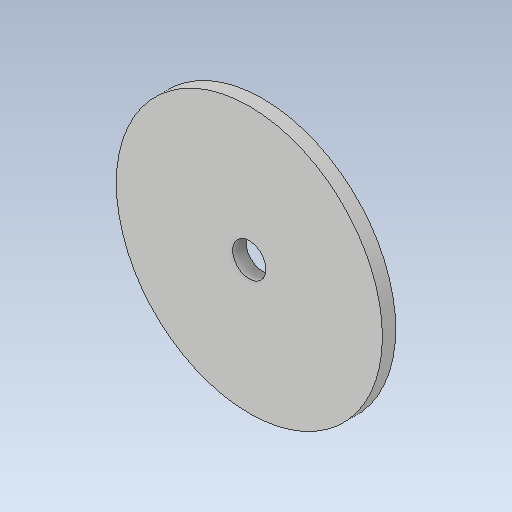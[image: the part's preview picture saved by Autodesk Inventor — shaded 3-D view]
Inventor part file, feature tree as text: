
AUTODESK INVENTOR PART (.ipt)
format: ipt  version: 2020 (Build 240168000, 168)  size: 95,232 bytes
history: native  units: mm
features: other x1, extrude x1, sketch x1
ambient origin geometry x8: Origin, YZ Plane, XZ Plane, XY Plane, X Axis, Y Axis, Z Axis, Center Point
bodies: Body1 (feature_tree)
feature tree (3):
  other  "Твердое тело1"
  extrude  "Выдавливание1"  Depth=5.0mm
  sketch  "Эскиз1"
